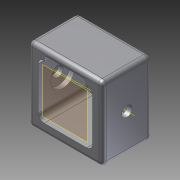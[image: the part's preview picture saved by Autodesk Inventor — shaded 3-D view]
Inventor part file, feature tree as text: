
AUTODESK INVENTOR PART (.ipt)
format: ipt  version: 2012 (Build 160160000, 160)  size: 216,576 bytes
history: native  units: mm
features: reference x9, extrude x5, sketch x5, fillet x4, plane x1, other x1, projected_geometry x1
ambient origin geometry x8: Origin, YZ Plane, XZ Plane, XY Plane, X Axis, Y Axis, Z Axis, Center Point
bodies: Solid1 (feature_tree)
feature tree (26):
  plane  "Work Plane1"
  extrude  "Extrusion1"  Depth=0.3mm
  extrude  "Extrusion2"  Depth=5.0mm
  fillet  "Fillet1"  Radius=5.0mm
  extrude  "Extrusion3"  Depth=25.0mm TaperAngle=0.0deg
  extrude  "Extrusion4"  Depth=0.3mm
  extrude  "Extrusion5"  Depth=25.0mm TaperAngle=0.0deg
  fillet  "Fillet2"  Radius=1.0mm
  fillet  "Fillet3"  Radius=12.3mm
  fillet  "Fillet4"  Radius=2.5mm
  other  "Work Axis1"
  sketch  "Sketch2"  dims[d3=0.3mm d4=0.3mm]
  reference  "Reference12"
  reference  "Reference13"
  reference  "Reference14"
  reference  "Reference15"
  sketch  "Sketch3"  dims[d5=0.3mm d6=5.0mm d7=5.0mm]
  reference  "Reference16"
  reference  "Reference17"
  reference  "Reference18"
  reference  "Reference19"
  reference  "Reference20"
  sketch  "Sketch4"  dims[d8=5.0mm d9=25.0mm d10=0.0mm]
  projected_geometry  "Projected Loop1"
  sketch  "Sketch5"  dims[d11=0.3mm d12=0.3mm]
  sketch  "Sketch6"  dims[d13=0.3mm d14=25.0mm d15=0.0mm d16=1.0mm d17=12.3mm d18=2.5mm d19=0.0mm d20=5.3mm d21=3.0mm d22=0.0mm d23=2.5mm d24=0.0mm d25=2.0mm d26=3.0mm d27=2.0mm]
